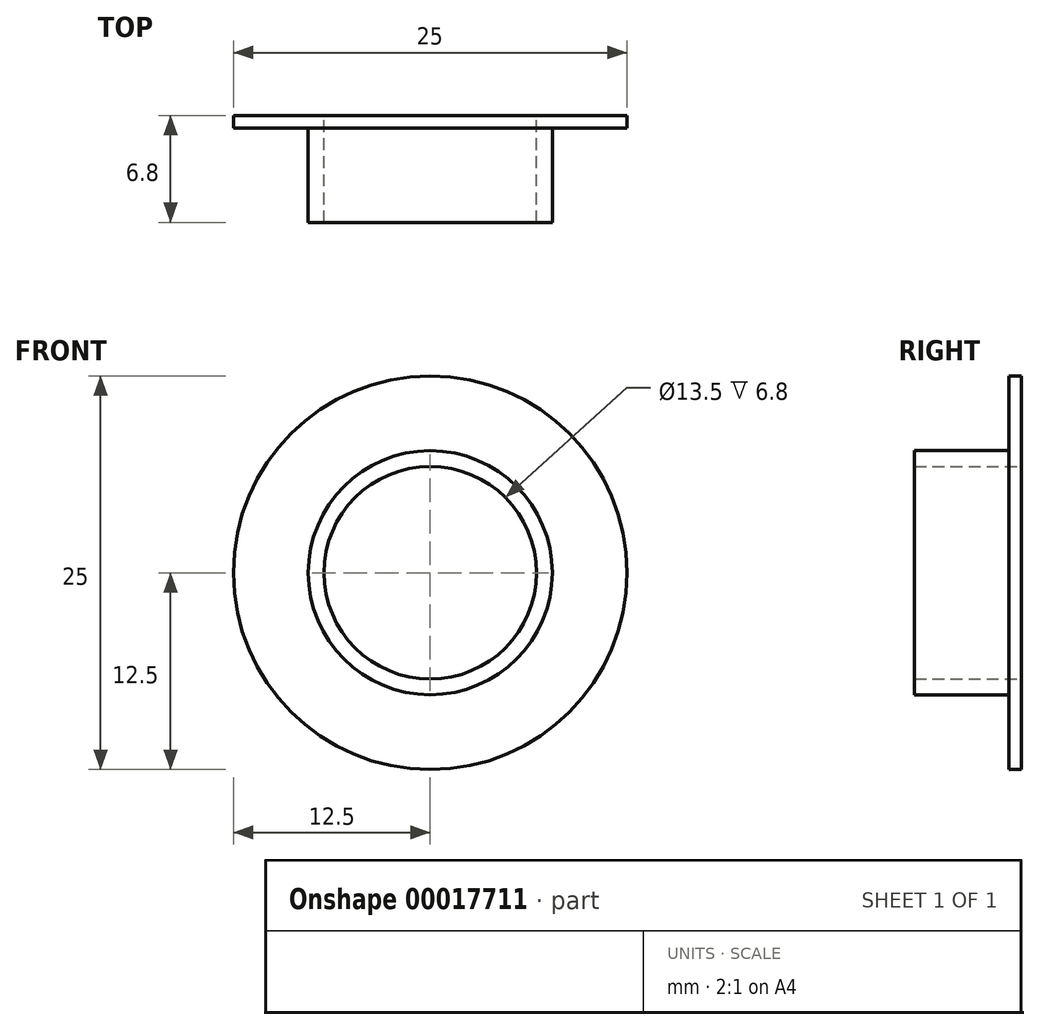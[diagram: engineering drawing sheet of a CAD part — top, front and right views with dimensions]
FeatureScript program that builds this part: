
annotation { "Feature Type Name" : "Feature", "Feature Type Description" : "" }
export const myFeature = defineFeature(function(context is Context, id is Id, definition is map)
    precondition{}
    {
        {
            var Q0;
            Q0=qCreatedBy(makeId("Front.planeOp"),FACE);
            var sketch = newSketch(context, id + "F0", { "sketchPlane" : qUnion([Q0])});
            skCircle(sketch, "E0", {"center": v(0, 0) * mm, "radius": 12.5 * mm});
            skSolve(sketch);
        }
        {
            var Q0;
            Q0=makeQuery(id+"F0.imprint","IMPRINT",FACE,{"disambiguationData":[TD([[makeQuery(id+"F0.imprint","IMPRINT",EDGE,{"derivedFrom":sQuery(id+"F0.wireOp",EDGE,"E0")}),1.0]])]});
            extrude(context, id + "F1", {"entities" : qUnion([Q0]), "depth" : 0.8 * mm});
        }
        {
            var Q0;
            Q0=makeQuery(id+"F1.opExtrude","CAP_FACE",FACE,{"disambiguationData":[OSD([sQuery(id+"F0.wireOp",EDGE,"E0")])],"isStart":false});
            var sketch = newSketch(context, id + "F2", { "sketchPlane" : qUnion([Q0])});
            skSolve(sketch);
        }
        {
            var Q0;
            Q0=makeQuery(id+"F2.imprint","IMPRINT",FACE,{"disambiguationData":[TD([[makeQuery(id+"F2.imprint","IMPRINT",EDGE,{"derivedFrom":makeQuery(id+"F1.opExtrude","CAP_EDGE",EDGE,{"disambiguationData":[OSD([sQuery(id+"F0.wireOp",EDGE,"E0")])],"isStart":false})}),1.0]])]});
            var sketch = newSketch(context, id + "F3", { "sketchPlane" : qUnion([Q0])});
            skCircle(sketch, "E1", {"center": v(0, 0) * mm, "radius": 6.75 * mm});
            skCircle(sketch, "E2.0", {"center": v(0, 0) * mm, "radius": 7.75 * mm});
            skSolve(sketch);
        }
        {
            var Q0;
            Q0 = qSketchRegion(id + "F3", true);
            extrude(context, id + "F4", {"entities" : qUnion([Q0]), "operationType" : NewBodyOperationType.ADD, "depth" : 6 * mm});
        }
        {
            var Q0;
            Q0=makeQuery(id+"F2.imprint","IMPRINT",FACE,{"disambiguationData":[TD([[makeQuery(id+"F2.imprint","IMPRINT",EDGE,{"derivedFrom":makeQuery(id+"F1.opExtrude","CAP_EDGE",EDGE,{"disambiguationData":[OSD([sQuery(id+"F0.wireOp",EDGE,"E0")])],"isStart":false})}),1.0]])]});
            var sketch = newSketch(context, id + "F5", { "sketchPlane" : qUnion([Q0])});
            skCircle(sketch, "E3", {"center": v(0, 0) * mm, "radius": 6.75 * mm});
            skSolve(sketch);
        }
        {
            var Q0;
            Q0 = qSketchRegion(id + "F5", true);
            extrude(context, id + "F6", {"entities" : qUnion([Q0]), "operationType" : NewBodyOperationType.REMOVE, "endBound" : BoundingType.THROUGH_ALL, "oppositeDirection" : true, "depth" : 25 * mm});
        }
    });
